# Revit family: NBS_Allermuir_DmstcChrs_Mote_Sofa120
name_source: partatom
category: Furniture
revit_build: Autodesk Revit 2016 (Build: 20150220_1215(x64)
units: mm (PartAtom-declared; Revit-internal decimal feet)

## family parameters
Always vertical = Yes
Cut with Voids When Loaded = No
Room Calculation Point = No
Shared = No
Work Plane-Based = No

## types (2) — shared parameters
AssetType = Moveable
Category = Pr_40_50_12_22:Dining chairs
Depth = 750 mm  [stored 2.46063 ft]
DurationUnit = year
ExpectedLife = 5
FrameColourOptions = Flint grey, mineral sand, mellow yellow, orange crush
FrameHeight = 246 mm  [stored 0.807087 ft]
FrameMountingMaterial = NBS_Concept
FramesColour = Black
FramesFinish = Powder coat
FramesMaterial = Aluminium
IfcExportAs = IfcFurnitureType
IfcExportType = SOFA
IsBuiltIn = No
JoiningArmOffset = 15 mm  [stored 0.0492126 ft]
ManufacturerName = Allermuir
ManufacturerURL = http://www.thesenatorgroup.com
NBSCertification = www.nationalbimlibrary.com/cert/ovpm3n3z
NBSDescription = Domestic chairs
NBSReference = 45-35-20/365
NominalDepth = 2040 mm
NominalHeight = 835 mm
NominalLength = 1030 mm  [stored 3.37927 ft]
NominalWidth = 2040 mm
ProductInformation = http://www.thesenatorgroup.com
ScreenFinishMaterial = NBS_Concept
ScreenHeight = 1030 mm  [stored 3.37927 ft]
SeatAngle = 120.00°
SeatArmRestHeight = 604 mm  [stored 1.98163 ft]
SeatEndRestOffset = 65 mm  [stored 0.213255 ft]
SeatFrameMaterial = NBS_Concept
SeatFrameWidth = 50 mm  [stored 0.164042 ft]
SeatLegOffset = 165 mm
SeatOverallWidth = 2130 mm  [stored 6.98819 ft]
SeatPowerSupplyMaterial = NBS_Concept
SeatScreenHeight = 1325 mm  [stored 4.34711 ft]
SeatingArmRestMaterial = NBS_Concept
SeatingHeight = 468 mm  [stored 1.53543 ft]
SeatingSeatMaterial = NBS_Concept
SeatsAndBacksFinish = Two-tone upholstery
SeatsAndBacksMaterial = Upholstered
Status = UNSET
Uniclass2015Code = Pr_40_50_12_22
Uniclass2015Title = Dining chairs
Uniclass2015Version = Products v1.9
Version = 1
WarrantyDescription = Allermuir warrant that its manufactured products are free from manufacturing defects in materials or workmanship for a period of five years
WarrantyDurationParts = 5
WarrantyDurationUnit = year
zero-valued in all types: HighestSeatingHeight, LowestSeatingHeight

## per-type parameters (varying)
| type | BIMObjectName | Description | Features | HasScreen | ModelReference | Name | OptionalAccessories | Size |
| MTE-SF120 | NBS_Allermuir_DomesticChairs_Mote_MTE-SF120 | 120° sofa | Fully upholstered, cast aluminium legs and aluminium perimeter frame finished in black powder coat, plastic glides with leveling adjustment, aluminium frame available in flint grey, mineral sand, mellow yellow or orange crush powder coat, two-tone upholstery | No | Mote sofa | DomesticChairs_Mote_MTE-SF120_Allermuir | 1 x front facing frame intergrated power unit with 2 x powered USB and 1 x power socket, 2 x rear facing frame intergrated power unit with 2 x powered USB and 1 x power socket | 1030 x 2040 x 835 mm |
| MTE-BSS120 | NBS_Allermuir_DomesticChairs_Mote_MTE-BSS120 | 120° angled sofa with rear screen | Rear screens, fully upholstered, cast aluminium legs and aluminium perimeter frame finished in black powder coat, plastic glides with leveling adjustment, aluminium frame available in flint grey, mineral sand, mellow yellow or orange crush powder coat, two-tone upholstery | Yes | Mote with rear screen | DomesticChairs_Mote_MTE-BSS120_Allermuir | 1 x front facing frame intergrated power unit 2 x powered USB and 1 x power socket, 2 x rear facing frame intergrated power unit 2 x powered USB and 1 x power socket | 2040 x 1030 x 1310 mm |

note: column(s) folded — value = type name in every type: ModelNumber

note: [stored X ft] marks values corroborated as IEEE doubles in the binary element streams (Revit-internal decimal feet)

## geometry (parser evidence)
native form markers: Sweep x9
no freeform markers — native parametric forms only
